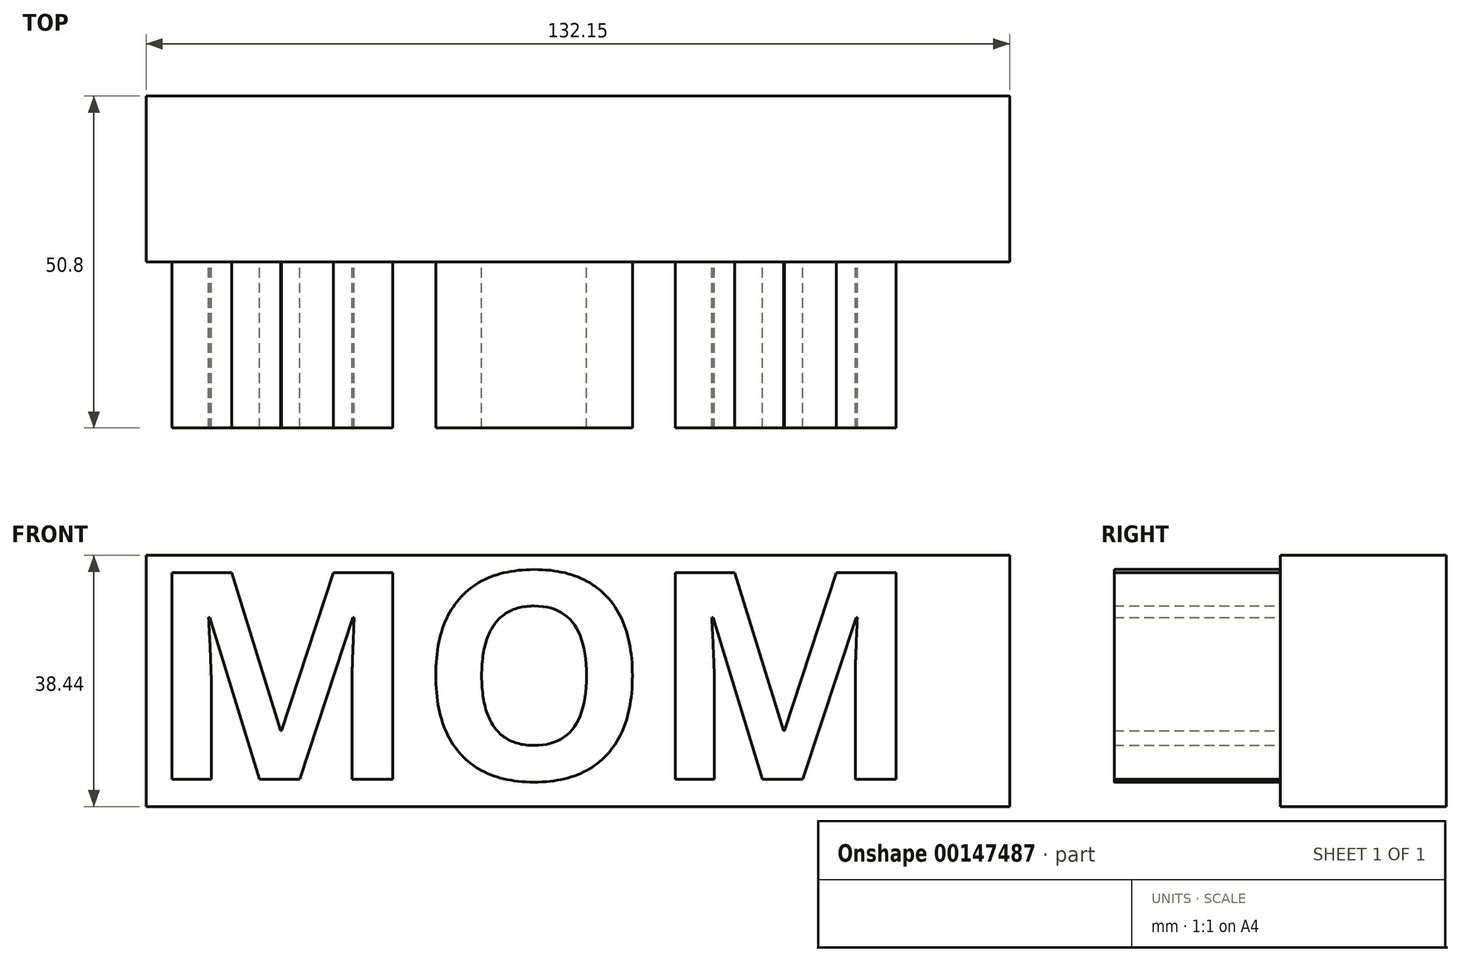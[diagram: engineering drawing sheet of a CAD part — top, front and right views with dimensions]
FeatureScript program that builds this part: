
annotation { "Feature Type Name" : "Feature", "Feature Type Description" : "" }
export const myFeature = defineFeature(function(context is Context, id is Id, definition is map)
    precondition{}
    {
        {
            var Q0;
            Q0=qCreatedBy(makeId("Front.planeOp"),FACE);
            var sketch = newSketch(context, id + "F0", { "sketchPlane" : qUnion([Q0])});
            skLineSegment(sketch, "E0.bottom", {"start": v(-37.55, 21) * mm, "end": v(43.8, 21) * mm});
            skLineSegment(sketch, "E0.top", {"start": v(-37.55, -17.43) * mm, "end": v(43.8, -17.43) * mm});
            skLineSegment(sketch, "E0.left", {"start": v(-37.55, 21) * mm, "end": v(-37.55, -17.43) * mm});
            skLineSegment(sketch, "E0.right", {"start": v(43.8, 21) * mm, "end": v(43.8, -17.43) * mm});
            skSolve(sketch);
        }
        {
            var Q0;
            Q0 = qSketchRegion(id + "F0", true);
            extrude(context, id + "F1", {"entities" : qUnion([Q0]), "depth" : 25.4 * mm});
        }
        {
            var Q0;
            Q0=makeQuery(id+"F1.opExtrude","CAP_FACE",FACE,{"disambiguationData":[OSD([sQuery(id+"F0.wireOp",EDGE,"E0.bottom"),sQuery(id+"F0.wireOp",EDGE,"E0.top"),sQuery(id+"F0.wireOp",EDGE,"E0.left"),sQuery(id+"F0.wireOp",EDGE,"E0.right")])],"isStart":false});
            var sketch = newSketch(context, id + "F2", { "sketchPlane" : qUnion([Q0])});
            skText(sketch, "E1", { "text": "MOM\n", "fontName": "OpenSans-Bold.ttf"});
            const initialGuessF2  = {"E1": [-0.03755, -0.01326, 1, 0, 0.03188]};
            skSetInitialGuess(sketch, initialGuessF2);
            skSolve(sketch);
        }
        {
            var Q0;
            Q0 = qSketchRegion(id + "F2", true);
            extrude(context, id + "F3", {"entities" : qUnion([Q0]), "operationType" : NewBodyOperationType.ADD, "depth" : 25.4 * mm});
        }
        {
            var Q0;
            Q0=makeQuery(id+"F1.opExtrude","SWEPT_FACE",FACE,{"disambiguationData":[OSD([sQuery(id+"F0.wireOp",EDGE,"E0.right")])]});
            extrude(context, id + "F4", {"entities" : qUnion([Q0]), "operationType" : NewBodyOperationType.ADD, "depth" : 25.4 * mm});
        }
        {
            var Q0;
            Q0=makeQuery(id+"F4.opExtrude","CAP_FACE",FACE,{"disambiguationData":[OSD([sQuery(id+"F0.wireOp",EDGE,"E0.right")])],"isStart":false});
            extrude(context, id + "F5", {"entities" : qUnion([Q0]), "operationType" : NewBodyOperationType.ADD, "depth" : 25.4 * mm});
        }
    });
